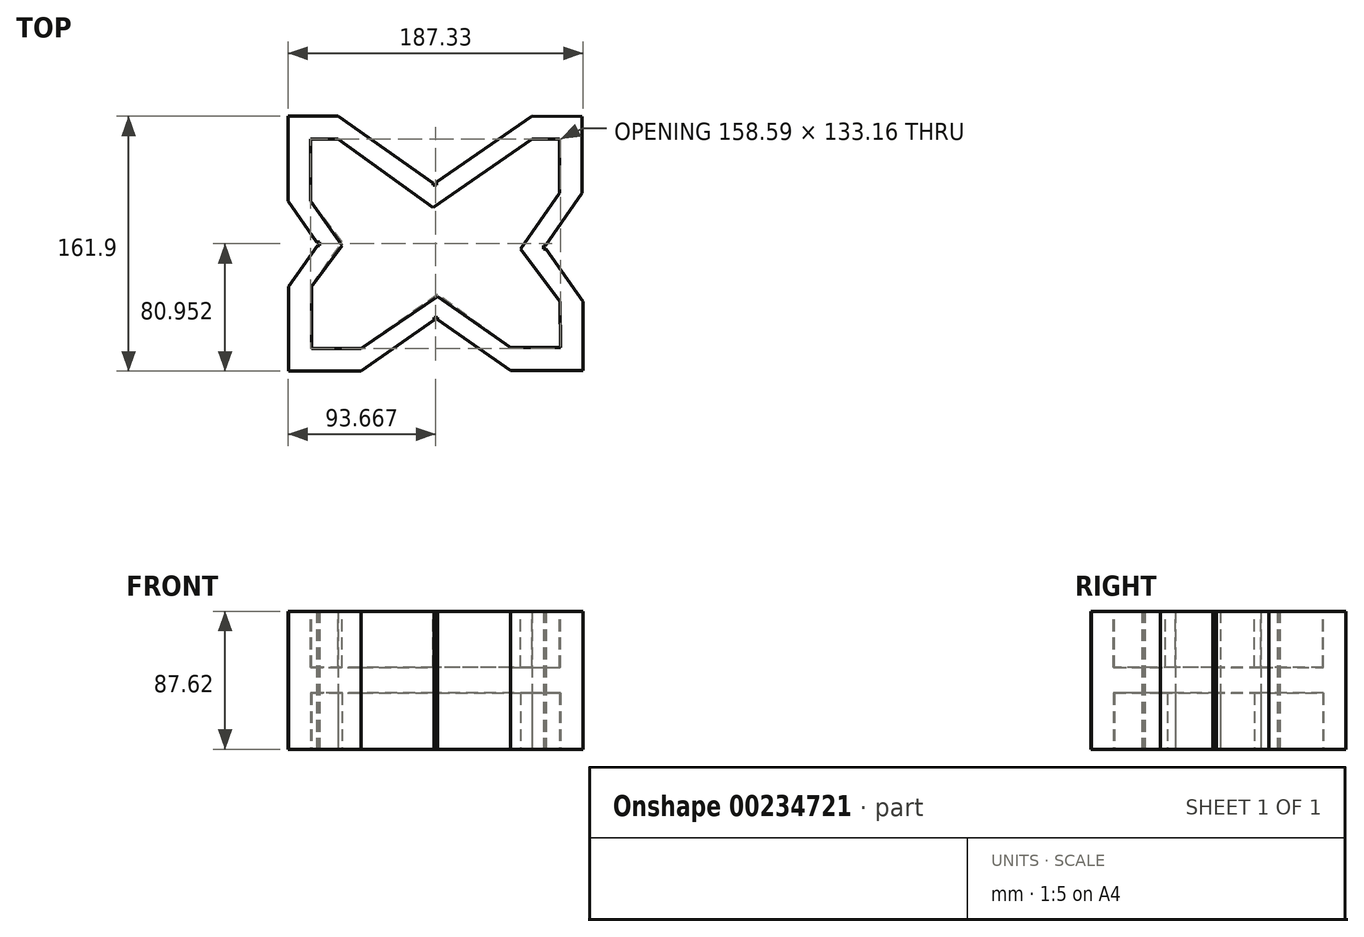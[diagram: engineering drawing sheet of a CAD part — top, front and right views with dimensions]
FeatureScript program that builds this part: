
annotation { "Feature Type Name" : "Feature", "Feature Type Description" : "" }
export const myFeature = defineFeature(function(context is Context, id is Id, definition is map)
    precondition{}
    {
        {
            var Q0;
            Q0=qCreatedBy(makeId("Top.planeOp"),FACE);
            var sketch = newSketch(context, id + "F0", { "sketchPlane" : qUnion([Q0])});
            skLineSegment(sketch, "E0", {"start": v(-59.25, 79.78) * mm, "end": v(-91, 79.78) * mm});
            skLineSegment(sketch, "E1", {"start": v(-91, 79.78) * mm, "end": v(-91, 26) * mm});
            skLineSegment(sketch, "E2", {"start": v(-91, 26) * mm, "end": v(-72.79, 0) * mm});
            skLineSegment(sketch, "E3", {"start": v(-72.79, 0) * mm, "end": v(-71, 0) * mm});
            skLineSegment(sketch, "E4", {"start": v(-71, 0) * mm, "end": v(-71, -2.29) * mm});
            skLineSegment(sketch, "E5", {"start": v(-71, -2.29) * mm, "end": v(-72.28, -2.29) * mm});
            skLineSegment(sketch, "E6", {"start": v(-72.28, -2.29) * mm, "end": v(-90.5, -28.3) * mm});
            skLineSegment(sketch, "E7", {"start": v(-90.5, -28.3) * mm, "end": v(-90.5, -82.12) * mm});
            skLineSegment(sketch, "E8", {"start": v(-90.5, -82.12) * mm, "end": v(-44.52, -82.12) * mm});
            skLineSegment(sketch, "E9", {"start": v(-44.52, -82.12) * mm, "end": v(1.78, -49.7) * mm});
            skLineSegment(sketch, "E10", {"start": v(1.78, -49.7) * mm, "end": v(1.78, -47.92) * mm});
            skLineSegment(sketch, "E11", {"start": v(1.78, -47.92) * mm, "end": v(4.06, -47.92) * mm});
            skLineSegment(sketch, "E12", {"start": v(4.06, -47.92) * mm, "end": v(4.06, -49.2) * mm});
            skLineSegment(sketch, "E13", {"start": v(4.06, -49.2) * mm, "end": v(50.36, -81.6) * mm});
            skLineSegment(sketch, "E14", {"start": v(50.36, -81.6) * mm, "end": v(96.33, -81.6) * mm});
            skLineSegment(sketch, "E15", {"start": v(96.33, -81.6) * mm, "end": v(96.33, -37.9) * mm});
            skLineSegment(sketch, "E16", {"start": v(96.33, -37.9) * mm, "end": v(73.02, -4.6) * mm});
            skPoint(sketch, "E17.end.orphan", {"position": v(73.02, 0) * mm});
            skLineSegment(sketch, "E18", {"start": v(73.02, -4.6) * mm, "end": v(71.24, -4.6) * mm});
            skLineSegment(sketch, "E19", {"start": v(71.24, -4.6) * mm, "end": v(71.24, -2.32) * mm});
            skLineSegment(sketch, "E20", {"start": v(71.24, -2.32) * mm, "end": v(72.51, -2.32) * mm});
            skLineSegment(sketch, "E21", {"start": v(72.51, -2.32) * mm, "end": v(95.82, 30.97) * mm});
            skLineSegment(sketch, "E22", {"start": v(95.82, 30.97) * mm, "end": v(95.82, 79.74) * mm});
            skLineSegment(sketch, "E23", {"start": v(-59.25, 79.78) * mm, "end": v(1.11, 37.52) * mm});
            skLineSegment(sketch, "E24", {"start": v(1.11, 37.52) * mm, "end": v(1.11, 36.25) * mm});
            skLineSegment(sketch, "E25", {"start": v(1.11, 36.25) * mm, "end": v(3.4, 36.25) * mm});
            skLineSegment(sketch, "E26", {"start": v(3.4, 36.25) * mm, "end": v(3.4, 38.02) * mm});
            skLineSegment(sketch, "E27", {"start": v(3.4, 38.02) * mm, "end": v(64.1, 79.78) * mm});
            skLineSegment(sketch, "E28", {"start": v(95.82, 79.74) * mm, "end": v(64.1, 79.78) * mm});
            skPoint(sketch, "E29.end.orphan", {"position": v(-14.63, 79.78) * mm});
            skSolve(sketch);
        }
        {
            var Q0;
            Q0=makeQuery(id+"F0.imprint","IMPRINT",FACE,{"disambiguationData":[TD([[makeQuery(id+"F0.imprint","IMPRINT",EDGE,{"derivedFrom":sQuery(id+"F0.wireOp",EDGE,"E0")}),1.0]])]});
            extrude(context, id + "F1", {"entities" : qUnion([Q0]), "endBound" : BoundingType.SYMMETRIC, "depth" : 87.63 * mm});
        }
        {
            var Q0;
            Q0=qCreatedBy(makeId("Top.planeOp"),FACE);
            cPlane(context, id + "F2", {"entities" : qUnion([Q0]), "cplaneType" : CPlaneType.OFFSET, "offset" : 44.2 * mm, "width" : 152.4 * mm, "height" : 152.4 * mm});
        }
        {
            var Q0;
            Q0=qCreatedBy(id+"F2.planeOp",FACE);
            var sketch = newSketch(context, id + "F3", { "sketchPlane" : qUnion([Q0])});
            skLineSegment(sketch, "E30", {"start": v(64.1, 65.3) * mm, "end": v(1.11, 21.77) * mm});
            skLineSegment(sketch, "E31", {"start": v(64.1, 65.3) * mm, "end": v(81.46, 65.37) * mm});
            skLineSegment(sketch, "E32", {"start": v(81.46, 65.37) * mm, "end": v(81.35, 30.97) * mm});
            skLineSegment(sketch, "E33", {"start": v(56.77, -4.6) * mm, "end": v(81.35, 30.97) * mm});
            skLineSegment(sketch, "E34", {"start": v(56.77, -4.6) * mm, "end": v(81.85, -37.9) * mm});
            skLineSegment(sketch, "E35", {"start": v(81.96, -67.24) * mm, "end": v(81.85, -37.9) * mm});
            skLineSegment(sketch, "E36", {"start": v(50.36, -67.13) * mm, "end": v(81.96, -67.24) * mm});
            skLineSegment(sketch, "E37", {"start": v(50.36, -67.13) * mm, "end": v(4.06, -34.72) * mm});
            skLineSegment(sketch, "E38", {"start": v(1.11, 21.77) * mm, "end": v(-59.25, 65.3) * mm});
            skLineSegment(sketch, "E39", {"start": v(-76.63, 65.41) * mm, "end": v(-59.25, 65.3) * mm});
            skLineSegment(sketch, "E40", {"start": v(-76.52, 26) * mm, "end": v(-76.63, 65.41) * mm});
            skLineSegment(sketch, "E41", {"start": v(-76.52, 26) * mm, "end": v(-56.53, -2.29) * mm});
            skLineSegment(sketch, "E42", {"start": v(-56.53, -2.29) * mm, "end": v(-76.01, -28.3) * mm});
            skLineSegment(sketch, "E43", {"start": v(-76.01, -28.3) * mm, "end": v(-76.12, -67.75) * mm});
            skLineSegment(sketch, "E44", {"start": v(-76.12, -67.75) * mm, "end": v(-44.52, -67.64) * mm});
            skLineSegment(sketch, "E45", {"start": v(-44.52, -67.64) * mm, "end": v(4.06, -34.72) * mm});
            skSolve(sketch);
        }
        {
            var Q0;
            Q0=makeQuery(id+"F3.imprint","IMPRINT",FACE,{"disambiguationData":[TD([[makeQuery(id+"F3.imprint","IMPRINT",EDGE,{"derivedFrom":sQuery(id+"F3.wireOp",EDGE,"E30")}),1.0]])]});
            extrude(context, id + "F4", {"entities" : qUnion([Q0]), "operationType" : NewBodyOperationType.REMOVE, "oppositeDirection" : true, "depth" : 36.04 * mm});
        }
        {
            var Q0;
            Q0=qCreatedBy(makeId("Top.planeOp"),FACE);
            cPlane(context, id + "F5", {"entities" : qUnion([Q0]), "cplaneType" : CPlaneType.OFFSET, "offset" : 44.2 * mm, "oppositeDirection" : true, "width" : 152.4 * mm, "height" : 152.4 * mm});
        }
        {
            var Q0;
            Q0=qCreatedBy(id+"F5.planeOp",FACE);
            var sketch = newSketch(context, id + "F6", { "sketchPlane" : qUnion([Q0])});
            skLineSegment(sketch, "E46", {"start": v(-76.12, -67.75) * mm, "end": v(-44.52, -67.64) * mm});
            skLineSegment(sketch, "E47", {"start": v(-44.52, -67.64) * mm, "end": v(4.06, -33.45) * mm});
            skLineSegment(sketch, "E48", {"start": v(4.06, -33.45) * mm, "end": v(50.36, -67.13) * mm});
            skLineSegment(sketch, "E49", {"start": v(50.36, -67.13) * mm, "end": v(81.96, -67.24) * mm});
            skLineSegment(sketch, "E50", {"start": v(81.96, -67.24) * mm, "end": v(81.85, -37.9) * mm});
            skLineSegment(sketch, "E51", {"start": v(81.85, -37.9) * mm, "end": v(56.77, -4.6) * mm});
            skLineSegment(sketch, "E52", {"start": v(56.77, -4.6) * mm, "end": v(81.35, 30.97) * mm});
            skLineSegment(sketch, "E53", {"start": v(81.35, 30.97) * mm, "end": v(81.46, 65.37) * mm});
            skLineSegment(sketch, "E54", {"start": v(81.46, 65.37) * mm, "end": v(64.1, 65.3) * mm});
            skLineSegment(sketch, "E55", {"start": v(64.1, 65.3) * mm, "end": v(1.11, 21.77) * mm});
            skLineSegment(sketch, "E56", {"start": v(1.11, 21.77) * mm, "end": v(-59.25, 65.3) * mm});
            skLineSegment(sketch, "E57", {"start": v(-59.25, 65.3) * mm, "end": v(-76.63, 65.41) * mm});
            skLineSegment(sketch, "E58", {"start": v(-76.63, 65.41) * mm, "end": v(-76.52, 26) * mm});
            skLineSegment(sketch, "E59", {"start": v(-76.52, 26) * mm, "end": v(-56.53, 0) * mm});
            skLineSegment(sketch, "E60", {"start": v(-56.53, 0) * mm, "end": v(-76.01, -28.3) * mm});
            skLineSegment(sketch, "E61", {"start": v(-76.01, -28.3) * mm, "end": v(-76.12, -67.75) * mm});
            skSolve(sketch);
        }
        {
            var Q0;
            Q0=makeQuery(id+"F6.imprint","IMPRINT",FACE,{"disambiguationData":[TD([[makeQuery(id+"F6.imprint","IMPRINT",EDGE,{"derivedFrom":sQuery(id+"F6.wireOp",EDGE,"E46")}),1.0]])]});
            extrude(context, id + "F7", {"entities" : qUnion([Q0]), "operationType" : NewBodyOperationType.REMOVE, "depth" : 36.04 * mm});
        }
    });
